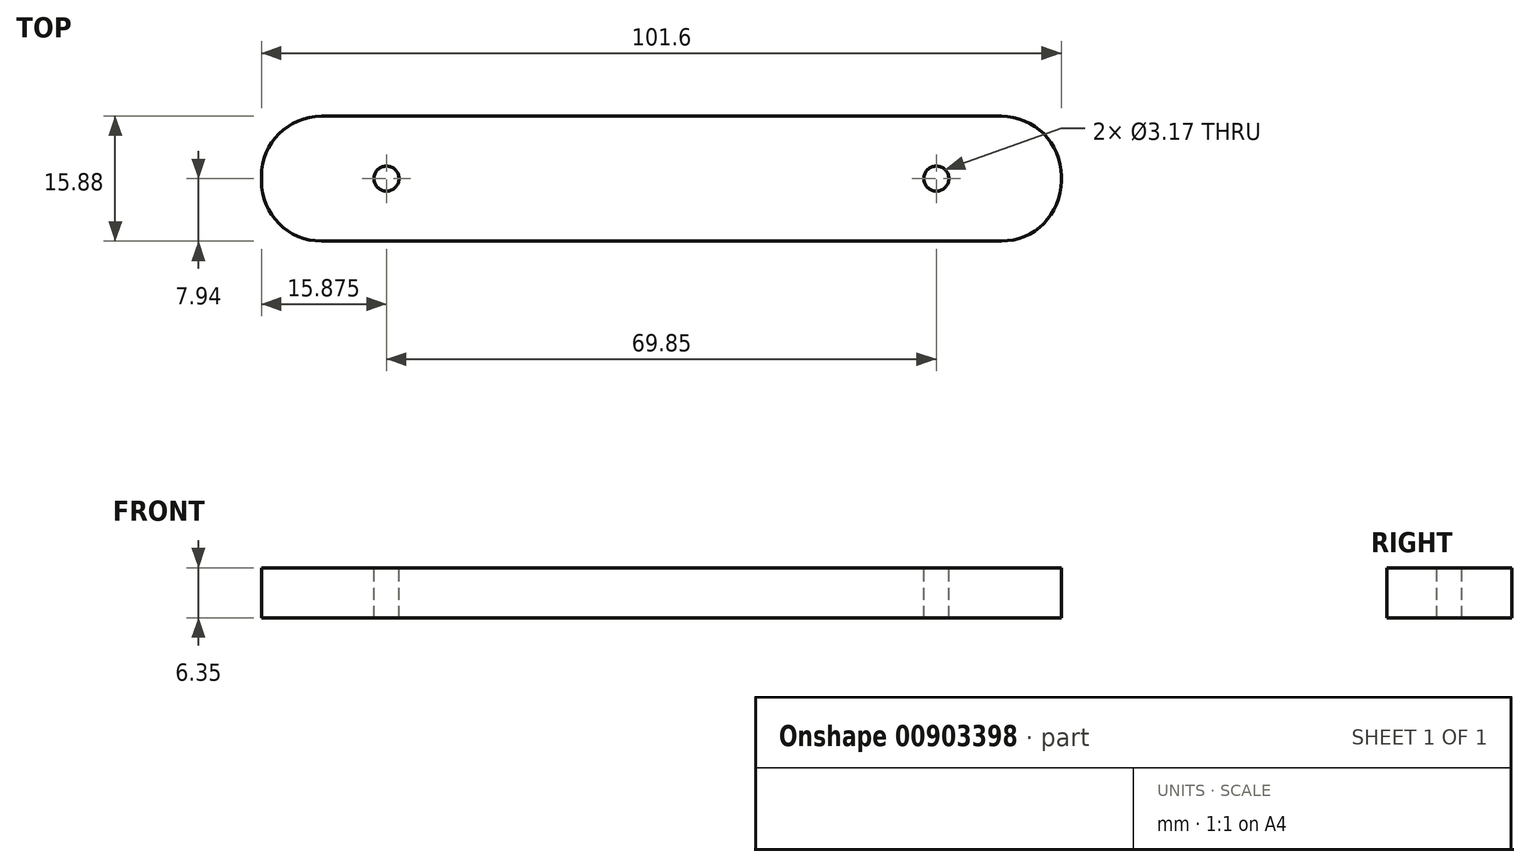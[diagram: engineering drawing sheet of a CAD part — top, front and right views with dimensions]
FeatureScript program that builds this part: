
annotation { "Feature Type Name" : "Feature", "Feature Type Description" : "" }
export const myFeature = defineFeature(function(context is Context, id is Id, definition is map)
    precondition{}
    {
        {
            var Q0;
            Q0=qCreatedBy(makeId("Top.planeOp"),FACE);
            var sketch = newSketch(context, id + "F0", { "sketchPlane" : qUnion([Q0])});
            skLineSegment(sketch, "E0", {"start": v(-50.8, 7.94) * mm, "end": v(-50.8, -7.94) * mm});
            skLineSegment(sketch, "E1", {"start": v(-50.8, -7.94) * mm, "end": v(50.8, -7.94) * mm});
            skLineSegment(sketch, "E2", {"start": v(-50.8, 7.94) * mm, "end": v(50.8, 7.94) * mm});
            skLineSegment(sketch, "E3", {"start": v(50.8, 7.94) * mm, "end": v(50.8, -7.94) * mm});
            skSolve(sketch);
        }
        {
            var Q0;
            Q0=makeQuery(id+"F0.imprint","IMPRINT",FACE,{"disambiguationData":[TD([[makeQuery(id+"F0.imprint","IMPRINT",EDGE,{"derivedFrom":sQuery(id+"F0.wireOp",EDGE,"E0")}),1.0]])]});
            extrude(context, id + "F1", {"entities" : qUnion([Q0]), "depth" : 6.35 * mm, "offsetDistance" : 25.4 * mm});
        }
        {
            var Q0;
            Q0=makeQuery(id+"F1.opExtrude","SWEPT_EDGE",EDGE,{"disambiguationData":[OSD([sQuery(id+"F0.wireOp",EDGE,"E0"),sQuery(id+"F0.wireOp",EDGE,"E2")])]});
            var Q1;
            Q1=makeQuery(id+"F1.opExtrude","SWEPT_EDGE",EDGE,{"disambiguationData":[OSD([sQuery(id+"F0.wireOp",EDGE,"E0"),sQuery(id+"F0.wireOp",EDGE,"E1")])]});
            var Q2;
            Q2=makeQuery(id+"F1.opExtrude","SWEPT_EDGE",EDGE,{"disambiguationData":[OSD([sQuery(id+"F0.wireOp",EDGE,"E2"),sQuery(id+"F0.wireOp",EDGE,"E3")])]});
            var Q3;
            Q3=makeQuery(id+"F1.opExtrude","SWEPT_EDGE",EDGE,{"disambiguationData":[OSD([sQuery(id+"F0.wireOp",EDGE,"E1"),sQuery(id+"F0.wireOp",EDGE,"E3")])]});
            fillet(context, id + "F2", {"entities" : qUnion([Q0, Q1, Q2, Q3]), "radius" : 7.62 * mm, "tangentPropagation" : true, "allowEdgeOverflow" : false});
        }
        {
            var Q0;
            Q0=makeQuery(id+"F1.opExtrude","CAP_FACE",FACE,{"disambiguationData":[OSD([sQuery(id+"F0.wireOp",EDGE,"E0"),sQuery(id+"F0.wireOp",EDGE,"E1"),sQuery(id+"F0.wireOp",EDGE,"E2"),sQuery(id+"F0.wireOp",EDGE,"E3")])],"isStart":false});
            var sketch = newSketch(context, id + "F3", { "sketchPlane" : qUnion([Q0])});
            skCircle(sketch, "E4", {"center": v(-34.93, 0) * mm, "radius": 1.59 * mm});
            skCircle(sketch, "E5", {"center": v(34.92, 0) * mm, "radius": 1.59 * mm});
            skSolve(sketch);
        }
        {
            var Q0;
            Q0 = qSketchRegion(id + "F3", true);
            extrude(context, id + "F4", {"entities" : qUnion([Q0]), "operationType" : NewBodyOperationType.REMOVE, "oppositeDirection" : true, "depth" : 25.4 * mm, "offsetDistance" : 25.4 * mm});
        }
    });
